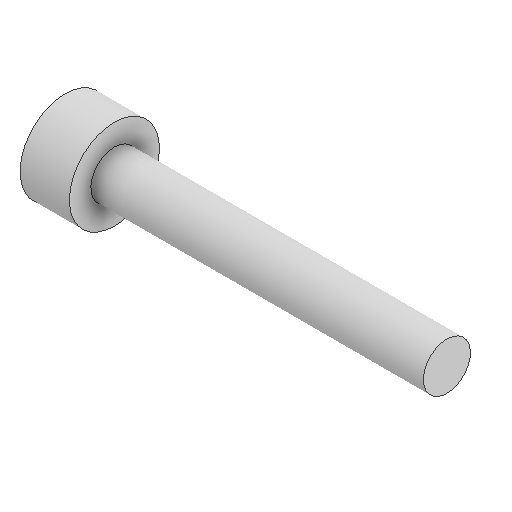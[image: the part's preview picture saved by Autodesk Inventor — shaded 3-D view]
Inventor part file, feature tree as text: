
AUTODESK INVENTOR PART (.ipt)
format: ipt  version: 2025 (Build 290162010, 162A)  size: 98,816 bytes
history: native  units: in
note: dims shown in document units (in); Inventor stores cm internally (conversion verified against a paired STEP export)
features: revolve x1, sketch x1
ambient origin geometry x8: Origin, YZ Plane, XZ Plane, XY Plane, X Axis, Y Axis, Z Axis, Center Point
bodies: Solid1 (feature_tree)
feature tree (2):
  revolve  "Revolution1"  [1 undecoded]
  sketch  "Sketch1"  dims[d0=0.21in d1=0.11in d2=0.115in d3=0.776in d4=90.0deg]
note: 1 required parameter value undecoded (feature->parameter linkage not recoverable at this tier; creation-order binding heuristic only, values carry confidence <= 0.55)
